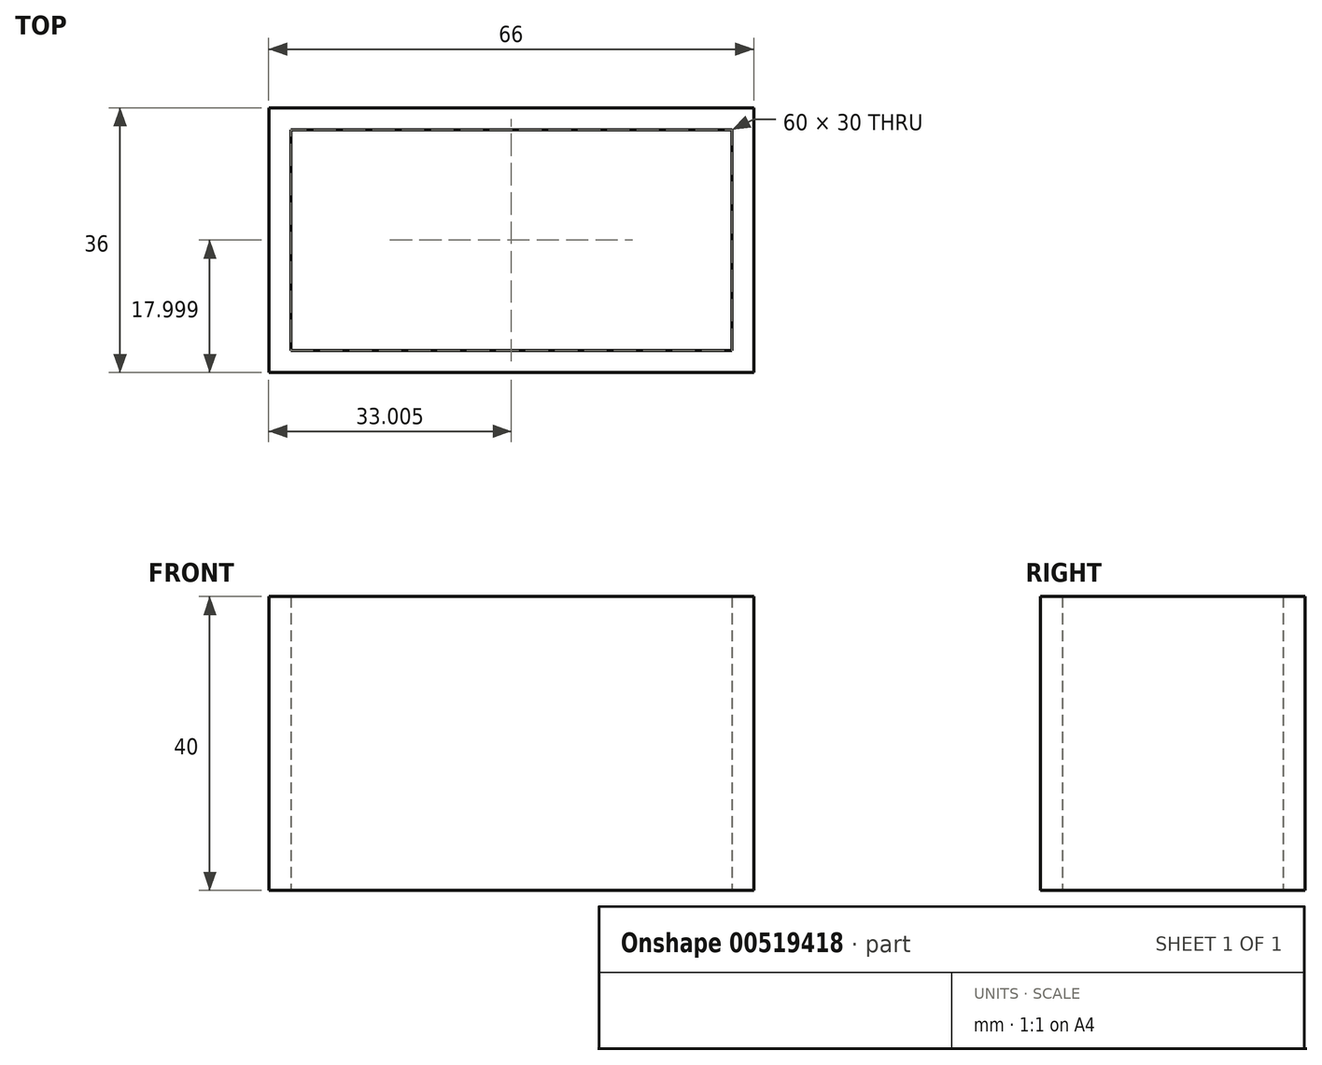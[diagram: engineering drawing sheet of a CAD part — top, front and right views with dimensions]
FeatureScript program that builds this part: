
annotation { "Feature Type Name" : "Feature", "Feature Type Description" : "" }
export const myFeature = defineFeature(function(context is Context, id is Id, definition is map)
    precondition{}
    {
        {
            var Q0;
            Q0=qCreatedBy(makeId("Top.planeOp"),FACE);
            var sketch = newSketch(context, id + "F0", { "sketchPlane" : qUnion([Q0])});
            skLineSegment(sketch, "E0.bottom", {"start": v(-25.6, 11.59) * mm, "end": v(34.4, 11.59) * mm});
            skLineSegment(sketch, "E0.top", {"start": v(-25.6, -18.41) * mm, "end": v(34.4, -18.41) * mm});
            skLineSegment(sketch, "E0.left", {"start": v(-25.6, 11.59) * mm, "end": v(-25.6, -18.41) * mm});
            skLineSegment(sketch, "E0.right", {"start": v(34.4, 11.59) * mm, "end": v(34.4, -18.41) * mm});
            skLineSegment(sketch, "E1.bottom", {"start": v(-28.6, 14.59) * mm, "end": v(37.4, 14.59) * mm});
            skLineSegment(sketch, "E1.top", {"start": v(-28.6, -21.41) * mm, "end": v(37.4, -21.41) * mm});
            skLineSegment(sketch, "E1.left", {"start": v(-28.6, 14.59) * mm, "end": v(-28.6, -21.41) * mm});
            skLineSegment(sketch, "E1.right", {"start": v(37.4, 14.59) * mm, "end": v(37.4, -21.41) * mm});
            skSolve(sketch);
        }
        {
            var Q0;
            Q0=makeQuery(id+"F0.imprint","IMPRINT",FACE,{"disambiguationData":[TD([[makeQuery(id+"F0.imprint","IMPRINT",EDGE,{"derivedFrom":sQuery(id+"F0.wireOp",EDGE,"E0.bottom")}),1.0]])]});
            extrude(context, id + "F1", {"entities" : qUnion([Q0]), "depth" : 40 * mm, "offsetDistance" : 25.4 * mm});
        }
    });
